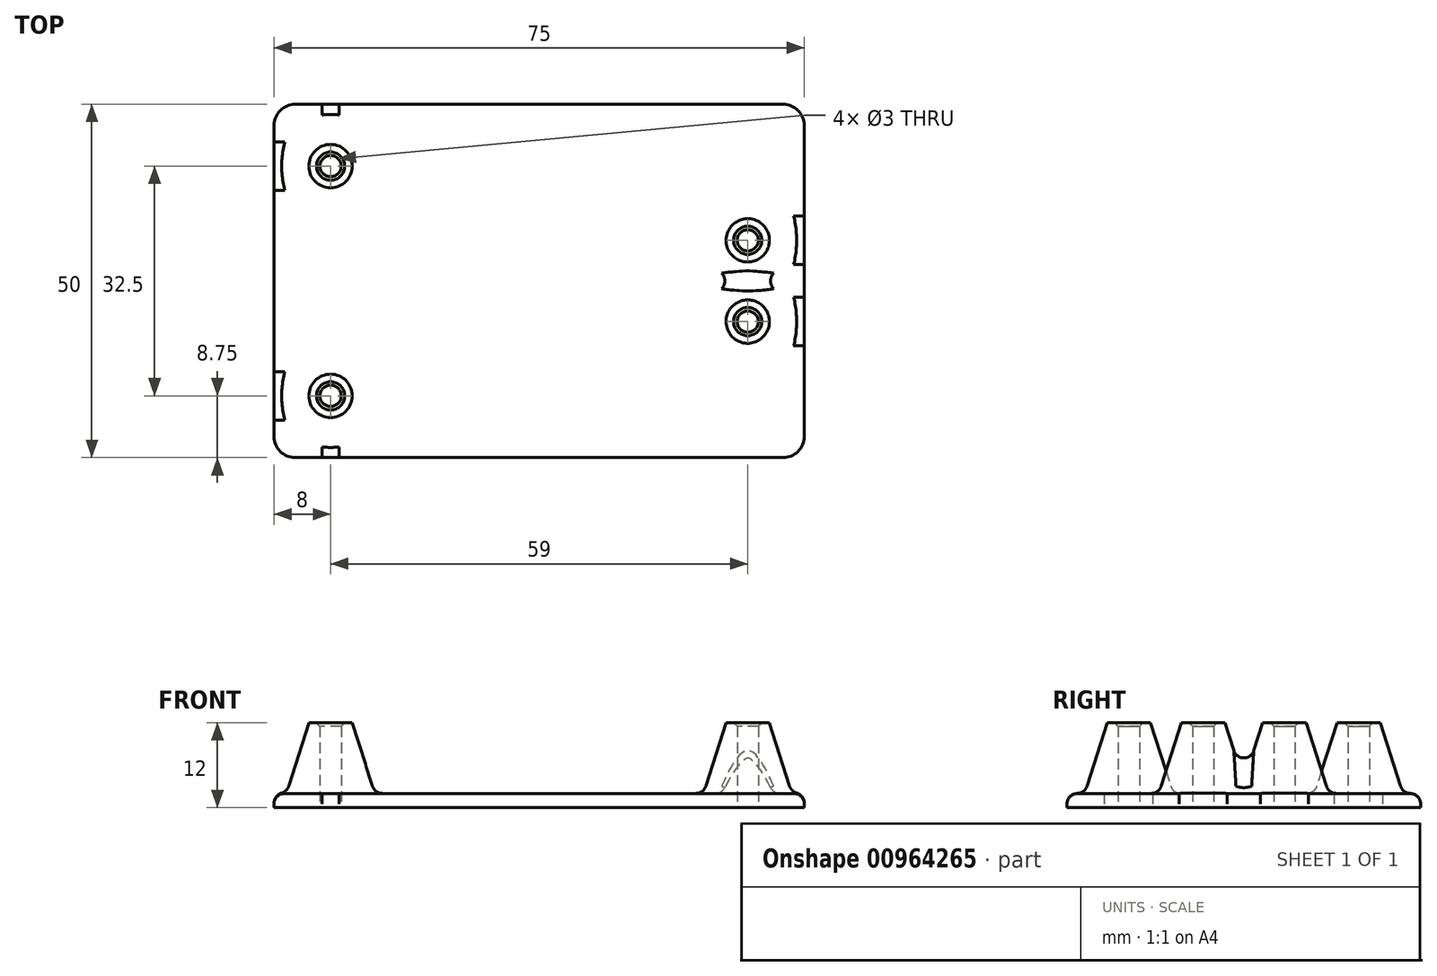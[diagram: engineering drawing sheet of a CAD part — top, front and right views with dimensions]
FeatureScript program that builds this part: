
annotation { "Feature Type Name" : "Feature", "Feature Type Description" : "" }
export const myFeature = defineFeature(function(context is Context, id is Id, definition is map)
    precondition{}
    {
        {
            var Q0;
            Q0=qCreatedBy(makeId("Top.planeOp"),FACE);
            var sketch = newSketch(context, id + "F0", { "sketchPlane" : qUnion([Q0])});
            skCircle(sketch, "E0", {"center": v(-29.5, 16.25) * mm, "radius": 1.5 * mm});
            skCircle(sketch, "E1", {"center": v(29.5, 5.75) * mm, "radius": 1.5 * mm});
            skLineSegment(sketch, "E2", {"start": v(0, 0) * mm, "end": v(-59.39, 0) * mm, "construction": true});
            skLineSegment(sketch, "E3", {"start": v(0, 0) * mm, "end": v(59.46, 0) * mm, "construction": true});
            skLineSegment(sketch, "E4.bottom", {"start": v(37.5, 25) * mm, "end": v(-37.5, 25) * mm});
            skLineSegment(sketch, "E4.top", {"start": v(37.5, -25) * mm, "end": v(-37.5, -25) * mm});
            skLineSegment(sketch, "E4.left", {"start": v(37.5, 25) * mm, "end": v(37.5, -25) * mm});
            skLineSegment(sketch, "E4.right", {"start": v(-37.5, 25) * mm, "end": v(-37.5, -25) * mm});
            skPoint(sketch, "E4.middle", {"position": v(0, 0) * mm});
            skCircle(sketch, "E5.MirrorC", {"center": v(-29.5, -16.25) * mm, "radius": 1.5 * mm});
            skCircle(sketch, "E6.MirrorC", {"center": v(29.5, -5.75) * mm, "radius": 1.5 * mm});
            skSolve(sketch);
        }
        {
            var Q0;
            Q0=qSketchRegion(id+"F0",true);
            extrude(context, id + "F1", {"entities" : qUnion([Q0]), "offsetDistance" : 25 * mm, "depth" : 2 * mm});
        }
        {
            var Q0;
            Q0=qCreatedBy(makeId("Top.planeOp"),FACE);
            var sketch = newSketch(context, id + "F2", { "sketchPlane" : qUnion([Q0])});
            skCircle(sketch, "E7.0", {"center": v(-29.5, 16.25) * mm, "radius": 1.5 * mm});
            skCircle(sketch, "E8.0", {"center": v(-29.5, -16.25) * mm, "radius": 1.5 * mm});
            skCircle(sketch, "E9.0", {"center": v(29.5, -5.75) * mm, "radius": 1.5 * mm});
            skCircle(sketch, "E10.0", {"center": v(29.5, 5.75) * mm, "radius": 1.5 * mm});
            skCircle(sketch, "E11", {"center": v(-29.5, 16.25) * mm, "radius": 2.75 * mm});
            skCircle(sketch, "E12", {"center": v(-29.5, -16.25) * mm, "radius": 2.75 * mm});
            skCircle(sketch, "E13", {"center": v(29.5, -5.75) * mm, "radius": 2.75 * mm});
            skCircle(sketch, "E14", {"center": v(29.5, 5.75) * mm, "radius": 2.75 * mm});
            skSolve(sketch);
        }
        {
            var Q0;
            Q0=qSketchRegion(id+"F2",true);
            extrude(context, id + "F3", {"entities" : qUnion([Q0]), "operationType" : NewBodyOperationType.ADD, "offsetDistance" : 25 * mm, "depth" : 12 * mm});
        }
        {
            var Q0;
            Q0=makeQuery(id+"F3.boolean.opBoolean","INTERSECT",EDGE,{"derivedFrom":[makeQuery(id+"F1.opExtrude","CAP_FACE",FACE,{"disambiguationData":[OSD([sQuery(id+"F0.wireOp",EDGE,"E0"),sQuery(id+"F0.wireOp",EDGE,"E1"),sQuery(id+"F0.wireOp",EDGE,"E4.bottom"),sQuery(id+"F0.wireOp",EDGE,"E4.top"),sQuery(id+"F0.wireOp",EDGE,"E4.left"),sQuery(id+"F0.wireOp",EDGE,"E4.right"),sQuery(id+"F0.wireOp",EDGE,"E5.MirrorC"),sQuery(id+"F0.wireOp",EDGE,"E6.MirrorC")])],"isStart":false}),makeQuery(id+"F3.opExtrude","SWEPT_FACE",FACE,{"disambiguationData":[OSD([sQuery(id+"F2.wireOp",EDGE,"E12")])]})]});
            var Q1;
            Q1=makeQuery(id+"F3.boolean.opBoolean","INTERSECT",EDGE,{"derivedFrom":[makeQuery(id+"F1.opExtrude","CAP_FACE",FACE,{"disambiguationData":[OSD([sQuery(id+"F0.wireOp",EDGE,"E0"),sQuery(id+"F0.wireOp",EDGE,"E1"),sQuery(id+"F0.wireOp",EDGE,"E4.bottom"),sQuery(id+"F0.wireOp",EDGE,"E4.top"),sQuery(id+"F0.wireOp",EDGE,"E4.left"),sQuery(id+"F0.wireOp",EDGE,"E4.right"),sQuery(id+"F0.wireOp",EDGE,"E5.MirrorC"),sQuery(id+"F0.wireOp",EDGE,"E6.MirrorC")])],"isStart":false}),makeQuery(id+"F3.opExtrude","SWEPT_FACE",FACE,{"disambiguationData":[OSD([sQuery(id+"F2.wireOp",EDGE,"E11")])]})]});
            var Q2;
            Q2=makeQuery(id+"F3.boolean.opBoolean","INTERSECT",EDGE,{"derivedFrom":[makeQuery(id+"F1.opExtrude","CAP_FACE",FACE,{"disambiguationData":[OSD([sQuery(id+"F0.wireOp",EDGE,"E0"),sQuery(id+"F0.wireOp",EDGE,"E1"),sQuery(id+"F0.wireOp",EDGE,"E4.bottom"),sQuery(id+"F0.wireOp",EDGE,"E4.top"),sQuery(id+"F0.wireOp",EDGE,"E4.left"),sQuery(id+"F0.wireOp",EDGE,"E4.right"),sQuery(id+"F0.wireOp",EDGE,"E5.MirrorC"),sQuery(id+"F0.wireOp",EDGE,"E6.MirrorC")])],"isStart":false}),makeQuery(id+"F3.opExtrude","SWEPT_FACE",FACE,{"disambiguationData":[OSD([sQuery(id+"F2.wireOp",EDGE,"E13")])]})]});
            var Q3;
            Q3=makeQuery(id+"F3.boolean.opBoolean","INTERSECT",EDGE,{"derivedFrom":[makeQuery(id+"F1.opExtrude","CAP_FACE",FACE,{"disambiguationData":[OSD([sQuery(id+"F0.wireOp",EDGE,"E0"),sQuery(id+"F0.wireOp",EDGE,"E1"),sQuery(id+"F0.wireOp",EDGE,"E4.bottom"),sQuery(id+"F0.wireOp",EDGE,"E4.top"),sQuery(id+"F0.wireOp",EDGE,"E4.left"),sQuery(id+"F0.wireOp",EDGE,"E4.right"),sQuery(id+"F0.wireOp",EDGE,"E5.MirrorC"),sQuery(id+"F0.wireOp",EDGE,"E6.MirrorC")])],"isStart":false}),makeQuery(id+"F3.opExtrude","SWEPT_FACE",FACE,{"disambiguationData":[OSD([sQuery(id+"F2.wireOp",EDGE,"E14")])]})]});
            chamfer(context, id + "F4", {"entities" : qUnion([Q0, Q1, Q2, Q3]), "chamferType" : ChamferType.TWO_OFFSETS, "width1" : 3.5 * mm, "oppositeDirection" : false, "width2" : 11 * mm, "tangentPropagation" : true});
        }
        {
            var Q0;
            {var subQ0=makeQuery(id+"F1.opExtrude","CAP_FACE",FACE,{"disambiguationData":[OSD([sQuery(id+"F0.wireOp",EDGE,"E0"),sQuery(id+"F0.wireOp",EDGE,"E1"),sQuery(id+"F0.wireOp",EDGE,"E4.bottom"),sQuery(id+"F0.wireOp",EDGE,"E4.top"),sQuery(id+"F0.wireOp",EDGE,"E4.left"),sQuery(id+"F0.wireOp",EDGE,"E4.right"),sQuery(id+"F0.wireOp",EDGE,"E5.MirrorC"),sQuery(id+"F0.wireOp",EDGE,"E6.MirrorC")])],"isStart":false});Q0=makeQuery(id+"F4.opChamfer","BLEND_EDGE",EDGE,{"blendedFrom":[makeQuery(id+"F3.boolean.opBoolean","INTERSECT",EDGE,{"derivedFrom":[subQ0,makeQuery(id+"F3.opExtrude","SWEPT_FACE",FACE,{"disambiguationData":[OSD([sQuery(id+"F2.wireOp",EDGE,"E11")])]})]}),subQ0],"blendedInto":[subQ0]});}
            var Q1;
            {var subQ0=makeQuery(id+"F1.opExtrude","CAP_FACE",FACE,{"disambiguationData":[OSD([sQuery(id+"F0.wireOp",EDGE,"E0"),sQuery(id+"F0.wireOp",EDGE,"E1"),sQuery(id+"F0.wireOp",EDGE,"E4.bottom"),sQuery(id+"F0.wireOp",EDGE,"E4.top"),sQuery(id+"F0.wireOp",EDGE,"E4.left"),sQuery(id+"F0.wireOp",EDGE,"E4.right"),sQuery(id+"F0.wireOp",EDGE,"E5.MirrorC"),sQuery(id+"F0.wireOp",EDGE,"E6.MirrorC")])],"isStart":false});Q1=makeQuery(id+"F4.opChamfer","BLEND_EDGE",EDGE,{"blendedFrom":[makeQuery(id+"F3.boolean.opBoolean","INTERSECT",EDGE,{"derivedFrom":[subQ0,makeQuery(id+"F3.opExtrude","SWEPT_FACE",FACE,{"disambiguationData":[OSD([sQuery(id+"F2.wireOp",EDGE,"E12")])]})]}),subQ0],"blendedInto":[subQ0]});}
            var Q2;
            {var subQ0=makeQuery(id+"F1.opExtrude","CAP_FACE",FACE,{"disambiguationData":[OSD([sQuery(id+"F0.wireOp",EDGE,"E0"),sQuery(id+"F0.wireOp",EDGE,"E1"),sQuery(id+"F0.wireOp",EDGE,"E4.bottom"),sQuery(id+"F0.wireOp",EDGE,"E4.top"),sQuery(id+"F0.wireOp",EDGE,"E4.left"),sQuery(id+"F0.wireOp",EDGE,"E4.right"),sQuery(id+"F0.wireOp",EDGE,"E5.MirrorC"),sQuery(id+"F0.wireOp",EDGE,"E6.MirrorC")])],"isStart":false});Q2=makeQuery(id+"F4.opChamfer","BLEND_EDGE",EDGE,{"blendedFrom":[makeQuery(id+"F3.boolean.opBoolean","INTERSECT",EDGE,{"derivedFrom":[subQ0,makeQuery(id+"F3.opExtrude","SWEPT_FACE",FACE,{"disambiguationData":[OSD([sQuery(id+"F2.wireOp",EDGE,"E13")])]})]}),subQ0],"blendedInto":[subQ0]});}
            var Q3;
            {var subQ0=makeQuery(id+"F1.opExtrude","CAP_FACE",FACE,{"disambiguationData":[OSD([sQuery(id+"F0.wireOp",EDGE,"E0"),sQuery(id+"F0.wireOp",EDGE,"E1"),sQuery(id+"F0.wireOp",EDGE,"E4.bottom"),sQuery(id+"F0.wireOp",EDGE,"E4.top"),sQuery(id+"F0.wireOp",EDGE,"E4.left"),sQuery(id+"F0.wireOp",EDGE,"E4.right"),sQuery(id+"F0.wireOp",EDGE,"E5.MirrorC"),sQuery(id+"F0.wireOp",EDGE,"E6.MirrorC")])],"isStart":false});Q3=makeQuery(id+"F4.opChamfer","BLEND_EDGE",EDGE,{"blendedFrom":[makeQuery(id+"F3.boolean.opBoolean","INTERSECT",EDGE,{"derivedFrom":[subQ0,makeQuery(id+"F3.opExtrude","SWEPT_FACE",FACE,{"disambiguationData":[OSD([sQuery(id+"F2.wireOp",EDGE,"E14")])]})]}),subQ0],"blendedInto":[subQ0]});}
            var Q4;
            {var subQ0=makeQuery(id+"F1.opExtrude","CAP_FACE",FACE,{"disambiguationData":[OSD([sQuery(id+"F0.wireOp",EDGE,"E0"),sQuery(id+"F0.wireOp",EDGE,"E1"),sQuery(id+"F0.wireOp",EDGE,"E4.bottom"),sQuery(id+"F0.wireOp",EDGE,"E4.top"),sQuery(id+"F0.wireOp",EDGE,"E4.left"),sQuery(id+"F0.wireOp",EDGE,"E4.right"),sQuery(id+"F0.wireOp",EDGE,"E5.MirrorC"),sQuery(id+"F0.wireOp",EDGE,"E6.MirrorC")])],"isStart":false});Q4=makeQuery(id+"F4.opChamfer","BLEND_EDGE",EDGE,{"blendedFrom":[makeQuery(id+"F3.boolean.opBoolean","INTERSECT",EDGE,{"derivedFrom":[subQ0,makeQuery(id+"F3.opExtrude","SWEPT_FACE",FACE,{"disambiguationData":[OSD([sQuery(id+"F2.wireOp",EDGE,"E13")])]})]}),makeQuery(id+"F3.boolean.opBoolean","INTERSECT",EDGE,{"derivedFrom":[subQ0,makeQuery(id+"F3.opExtrude","SWEPT_FACE",FACE,{"disambiguationData":[OSD([sQuery(id+"F2.wireOp",EDGE,"E14")])]})]})],"blendedInto":[]});}
            fillet(context, id + "F5", {"entities" : qUnion([Q0, Q1, Q2, Q3, Q4]), "radius" : 1.5 * mm, "tangentPropagation" : true, "allowEdgeOverflow" : false});
        }
        {
            var Q0;
            Q0=makeQuery(id+"F3.opExtrude","CAP_EDGE",EDGE,{"disambiguationData":[OSD([sQuery(id+"F2.wireOp",EDGE,"E8.0")])],"isStart":false});
            var Q1;
            Q1=makeQuery(id+"F3.opExtrude","CAP_EDGE",EDGE,{"disambiguationData":[OSD([sQuery(id+"F2.wireOp",EDGE,"E9.0")])],"isStart":false});
            var Q2;
            Q2=makeQuery(id+"F3.opExtrude","CAP_EDGE",EDGE,{"disambiguationData":[OSD([sQuery(id+"F2.wireOp",EDGE,"E10.0")])],"isStart":false});
            var Q3;
            Q3=makeQuery(id+"F3.opExtrude","CAP_EDGE",EDGE,{"disambiguationData":[OSD([sQuery(id+"F2.wireOp",EDGE,"E7.0")])],"isStart":false});
            chamfer(context, id + "F6", {"entities" : qUnion([Q0, Q1, Q2, Q3]), "width" : 0.5 * mm, "tangentPropagation" : true});
        }
        {
            var Q0;
            Q0=makeQuery(id+"F1.opExtrude","SWEPT_EDGE",EDGE,{"disambiguationData":[OSD([sQuery(id+"F0.wireOp",EDGE,"E4.top"),sQuery(id+"F0.wireOp",EDGE,"E4.right")])]});
            var Q1;
            Q1=makeQuery(id+"F1.opExtrude","SWEPT_EDGE",EDGE,{"disambiguationData":[OSD([sQuery(id+"F0.wireOp",EDGE,"E4.top"),sQuery(id+"F0.wireOp",EDGE,"E4.left")])]});
            var Q2;
            Q2=makeQuery(id+"F1.opExtrude","SWEPT_EDGE",EDGE,{"disambiguationData":[OSD([sQuery(id+"F0.wireOp",EDGE,"E4.bottom"),sQuery(id+"F0.wireOp",EDGE,"E4.left")])]});
            var Q3;
            Q3=makeQuery(id+"F1.opExtrude","SWEPT_EDGE",EDGE,{"disambiguationData":[OSD([sQuery(id+"F0.wireOp",EDGE,"E4.bottom"),sQuery(id+"F0.wireOp",EDGE,"E4.right")])]});
            fillet(context, id + "F7", {"entities" : qUnion([Q0, Q1, Q2, Q3]), "radius" : 3 * mm, "tangentPropagation" : true, "allowEdgeOverflow" : false});
        }
        {
            var Q0;
            Q0=makeQuery(id+"F1.opExtrude","CAP_EDGE",EDGE,{"disambiguationData":[OSD([sQuery(id+"F0.wireOp",EDGE,"E4.bottom")])],"isStart":false});
            fillet(context, id + "F8", {"entities" : qUnion([Q0]), "radius" : 1.5 * mm, "tangentPropagation" : true, "allowEdgeOverflow" : false});
        }
    });
